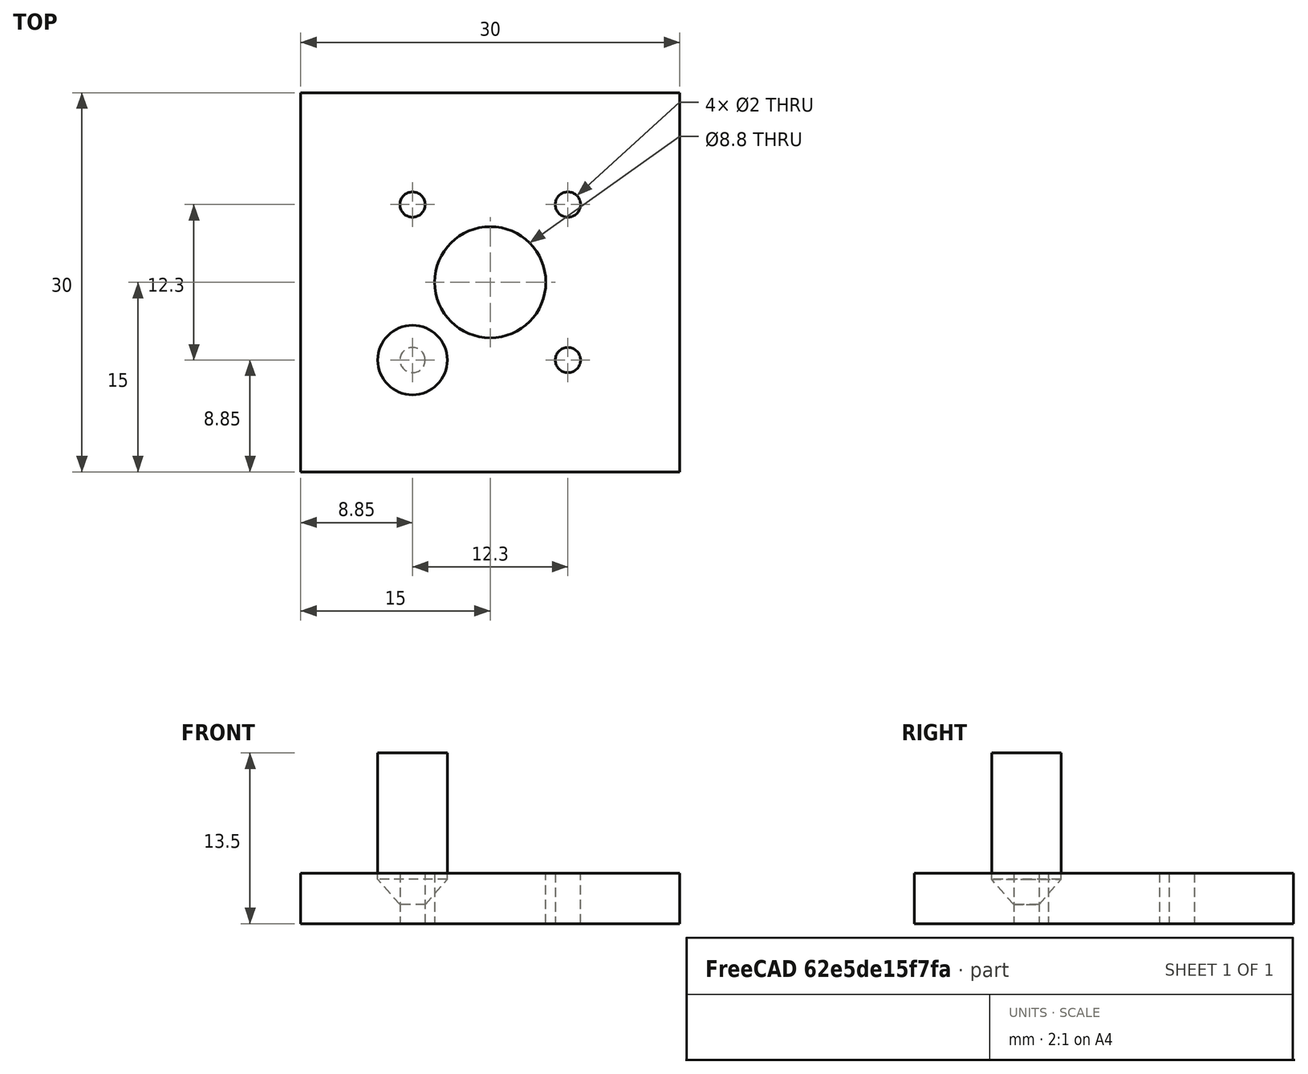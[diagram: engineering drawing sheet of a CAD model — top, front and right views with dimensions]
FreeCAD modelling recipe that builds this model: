
FCSTD DOCUMENT  (FreeCAD 0.19R0.19.2)
Label: motorMount003
License: All rights reserved
LicenseURL: http://en.wikipedia.org/wiki/All_rights_reserved
objects: Sketcher::SketchObject×1, Part::Extrusion×1, Part::Cone×1, Part::Cylinder×1, Part::Fuse×1
note: 5 computed .brp shape members not serialized (recipe doc carries the construction recipe); baked Part::Feature solids carry a one-line shape summary decoded from their .brp

FEATURE [Sketcher::SketchObject] Sketch
  FullyConstrained = true
  sketch-geometry (9):
    g0: Circle CenterX=6.15 CenterY=6.15 CenterZ=0 NormalX=0 NormalY=0 NormalZ=1 AngleXU=0 Radius=4.4
    g1: LineSegment StartX=-8.85 StartY=21.15 StartZ=0 EndX=21.15 EndY=21.15 EndZ=0
    g2: LineSegment StartX=21.15 StartY=21.15 StartZ=0 EndX=21.15 EndY=-8.85 EndZ=0
    g3: LineSegment StartX=-8.85 StartY=21.15 StartZ=0 EndX=-8.85 EndY=-8.85 EndZ=0
    g4: LineSegment StartX=-8.85 StartY=-8.85 StartZ=0 EndX=21.15 EndY=-8.85 EndZ=0
    g5: Circle CenterX=0 CenterY=12.3 CenterZ=0 NormalX=0 NormalY=0 NormalZ=1 AngleXU=0 Radius=1
    g6: Circle CenterX=12.3 CenterY=12.3 CenterZ=0 NormalX=0 NormalY=0 NormalZ=1 AngleXU=0 Radius=1
    g7: Circle CenterX=12.3 CenterY=0 CenterZ=0 NormalX=0 NormalY=0 NormalZ=1 AngleXU=0 Radius=1
    g8: Circle CenterX=0 CenterY=0 CenterZ=0 NormalX=0 NormalY=0 NormalZ=1 AngleXU=0 Radius=1
  constraints (18):
    c: Block(g0)
    c: Horizontal(g1)
    c: Distance(g1) = 30
    c: Vertical(g2)
    c: Block(g1)
    c: Distance(g2) = 30
    c: Coincident(g2,g1)
    c: Vertical(g3)
    c: Distance(g3) = 30
    c: Coincident(g3,g1)
    c: Block(g3)
    c: Block(g2)
    c: Coincident(g4,g3)
    c: Coincident(g4,g2)
    c: Block(g5)
    c: Block(g6)
    c: Block(g7)
    c: Block(g8)
FEATURE [Part::Extrusion] Extrude
  Base = -> Sketch
  Dir = (0,0,1)
  DirMode = 2
  FaceMakerClass = Part::FaceMakerBullseye
  LengthFwd = 4
  LengthRev = 0
  Solid = true
  Symmetric = false
FEATURE [Part::Cone] Cone
  Angle = 360
  AttacherType = Attacher::AttachEngine3D
  Height = 2
  Placement = pos=(0,0,1.5) rot=(0,0,1;0rad)
  Radius1 = 1
  Radius2 = 2.75
FEATURE [Part::Cylinder] Cylinder
  Angle = 360
  AttacherType = Attacher::AttachEngine3D
  Height = 10
  Placement = pos=(0,0,3.5) rot=(0,0,1;0rad)
  Radius = 2.75
FEATURE [Part::Fuse] Fusion  label="removeFromMainToCreateScrewChamfer"
  Base = -> Cone
  Tool = -> Cylinder
